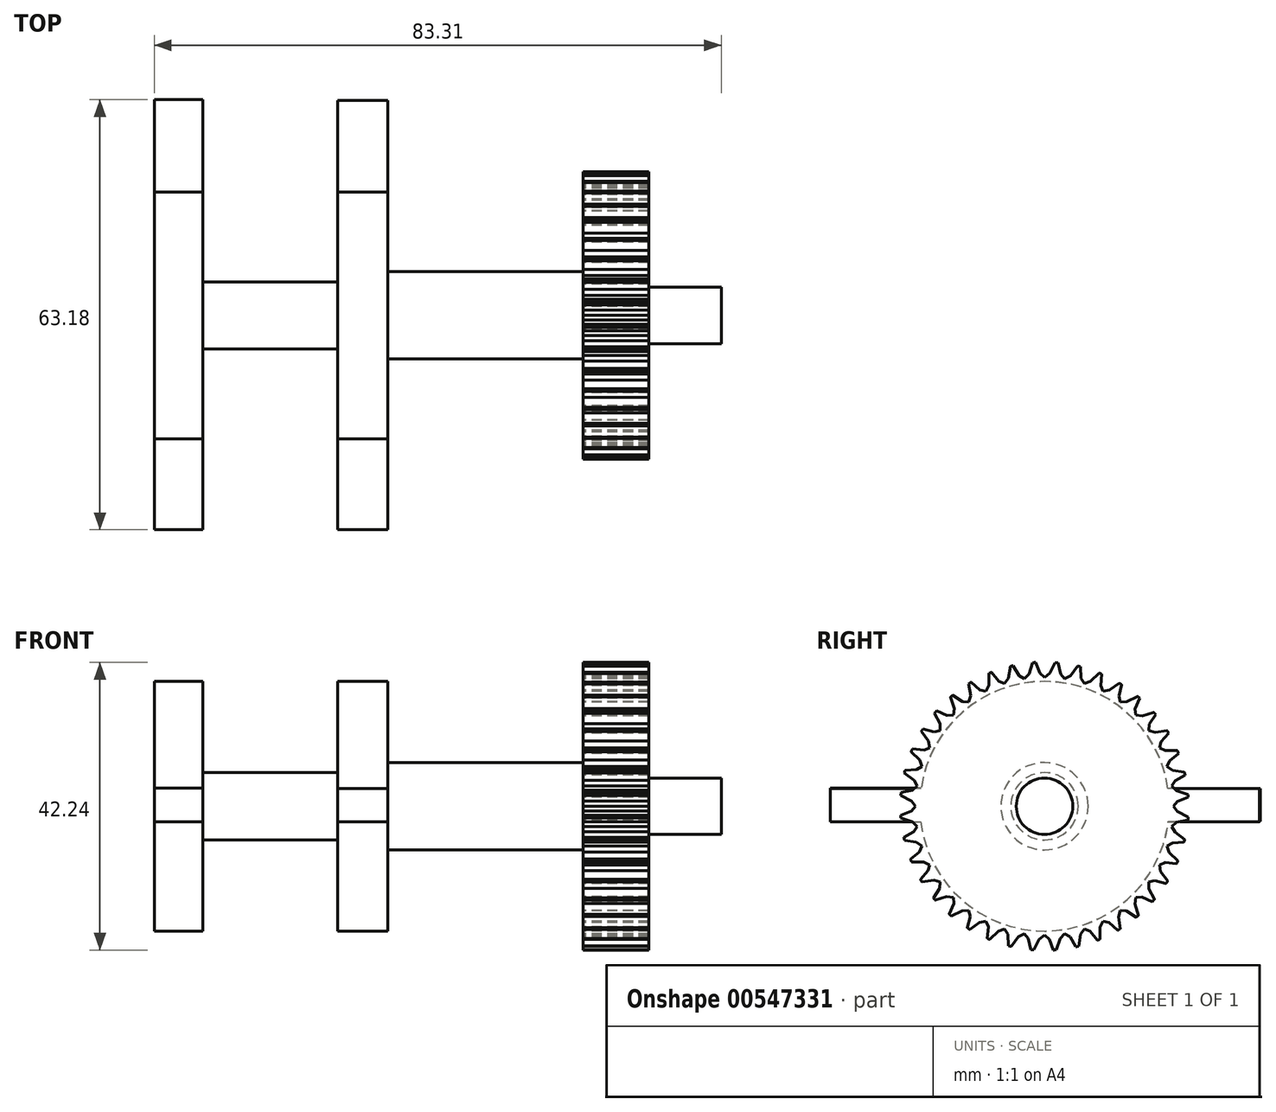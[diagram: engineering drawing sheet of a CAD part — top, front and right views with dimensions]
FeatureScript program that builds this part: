
annotation { "Feature Type Name" : "Feature", "Feature Type Description" : "" }
export const myFeature = defineFeature(function(context is Context, id is Id, definition is map)
    precondition{}
    {
        {
            var Q0;
            Q0=qCreatedBy(makeId("Right.planeOp"),FACE);
            var sketch = newSketch(context, id + "F0", { "sketchPlane" : qUnion([Q0])});
            skCircle(sketch, "E0", {"center": v(0, 0) * mm, "radius": 20.47 * mm});
            skLineSegment(sketch, "E1", {"start": v(0, -20.47) * mm, "end": v(0, -32.87) * mm});
            skLineSegment(sketch, "E2", {"start": v(0, -32.87) * mm, "end": v(-4.43, -32.81) * mm});
            skLineSegment(sketch, "E3", {"start": v(-4.43, -32.81) * mm, "end": v(-4.43, -19.99) * mm});
            skLineSegment(sketch, "E4.MirrorCS", {"start": v(0, 32.87) * mm, "end": v(-4.43, 32.81) * mm});
            skLineSegment(sketch, "E5.MirrorCS", {"start": v(-4.43, 32.81) * mm, "end": v(-4.43, 19.99) * mm});
            skLineSegment(sketch, "E6.MirrorCS", {"start": v(0, 20.47) * mm, "end": v(0, 32.87) * mm});
            skSolve(sketch);
        }
        {
            var Q0;
            {var subQ0=sQuery(id+"F0.wireOp",EDGE,"E0");var subQ1=makeQuery(id+"F0.imprint","INTERSECT",VERTEX,{"derivedFrom":[subQ0,sQuery(id+"F0.wireOp",EDGE,"ybv6XF9e-yQJ6-GcxN-1k9M-g7d4zqfCFwmI")]});Q0=makeQuery(id+"F0.imprint","IMPRINT",FACE,{"disambiguationData":[TD([[makeQuery(id+"F0.imprint","IMPRINT",EDGE,{"disambiguationData":[TD([[subQ1,1.0]])],"derivedFrom":subQ0}),1.0]])]});}
            var Q1;
            {var subQ0=sQuery(id+"F0.wireOp",EDGE,"ybv6XF9e-yQJ6-GcxN-1k9M-g7d4zqfCFwmI");Q1=makeQuery(id+"F0.imprint","IMPRINT",FACE,{"disambiguationData":[TD([[makeQuery(id+"F0.imprint","IMPRINT",EDGE,{"derivedFrom":subQ0}),-1.0]])]});}
            var Q2;
            {var subQ0=sQuery(id+"F0.wireOp",EDGE,"E1");Q2=makeQuery(id+"F0.imprint","IMPRINT",FACE,{"disambiguationData":[TD([[makeQuery(id+"F0.imprint","IMPRINT",EDGE,{"derivedFrom":subQ0}),-1.0]])]});}
            var Q3;
            Q3=makeQuery(id+"F0.imprint","IMPRINT",FACE,{"disambiguationData":[TD([[makeQuery(id+"F0.imprint","IMPRINT",EDGE,{"derivedFrom":sQuery(id+"F0.wireOp",EDGE,"E4.MirrorCS")}),1.0]])]});
            extrude(context, id + "F1", {"entities" : qUnion([Q0, Q1, Q2, Q3]), "depth" : 5.08 * mm, "offsetDistance" : 25.4 * mm});
        }
        {
            var Q0;
            Q0=makeQuery(id+"F1.opExtrude","CAP_FACE",FACE,{"disambiguationData":[OSD([sQuery(id+"F0.wireOp",EDGE,"E0"),sQuery(id+"F0.wireOp",EDGE,"ybv6XF9e-yQJ6-GcxN-1k9M-g7d4zqfCFwmI"),sQuery(id+"F0.wireOp",EDGE,"egRvkigp-FsvL-QF5D-I4YD-MoUuUeyJkvTS"),sQuery(id+"F0.wireOp",EDGE,"ktJIH1Pw-zPiB-Zv6z-c4OE-IvtrcdQjdgDW"),sQuery(id+"F0.wireOp",EDGE,"E1"),sQuery(id+"F0.wireOp",EDGE,"E2"),sQuery(id+"F0.wireOp",EDGE,"E3")])],"isStart":false});
            var sketch = newSketch(context, id + "F2", { "sketchPlane" : qUnion([Q0])});
            skCircle(sketch, "E7", {"center": v(0, 0) * mm, "radius": 22.86 * mm});
            skSolve(sketch);
        }
        {
            var Q0;
            {var subQ1=sQuery(id+"F0.wireOp",EDGE,"ybv6XF9e-yQJ6-GcxN-1k9M-g7d4zqfCFwmI");var subQ7=sQuery(id+"F0.wireOp",EDGE,"E0");var subQ8=makeQuery(id+"F1.opExtrude","CAP_EDGE",EDGE,{"disambiguationData":[OSD([subQ7]),TDD([makeQuery(id+"F0.imprint","IMPRINT",EDGE,{"disambiguationData":[TD([[makeQuery(id+"F0.imprint","INTERSECT",VERTEX,{"derivedFrom":[subQ7,subQ1]}),-1.0]])],"derivedFrom":subQ7})])],"isStart":false});Q0=makeQuery(id+"F2.imprint","IMPRINT",FACE,{"disambiguationData":[TD([[makeQuery(id+"F2.imprint","IMPRINT",EDGE,{"derivedFrom":subQ8}),-1.0]])]});}
            var Q1;
            {var subQ0=sQuery(id+"F0.wireOp",EDGE,"ybv6XF9e-yQJ6-GcxN-1k9M-g7d4zqfCFwmI");var subQ1=sQuery(id+"F0.wireOp",EDGE,"E0");var subQ3=makeQuery(id+"F1.opExtrude","CAP_EDGE",EDGE,{"disambiguationData":[OSD([subQ1]),TDD([makeQuery(id+"F0.imprint","IMPRINT",EDGE,{"disambiguationData":[TD([[makeQuery(id+"F0.imprint","INTERSECT",VERTEX,{"derivedFrom":[subQ1,subQ0]}),-1.0]])],"derivedFrom":subQ1})])],"isStart":false});Q1=makeQuery(id+"F2.imprint","IMPRINT",FACE,{"disambiguationData":[TD([[makeQuery(id+"F2.imprint","IMPRINT",EDGE,{"derivedFrom":subQ3}),1.0]])]});}
            var Q2;
            {var subQ1=sQuery(id+"F0.wireOp",EDGE,"ktJIH1Pw-zPiB-Zv6z-c4OE-IvtrcdQjdgDW");var subQ7=sQuery(id+"F0.wireOp",EDGE,"E0");var subQ8=makeQuery(id+"F1.opExtrude","CAP_EDGE",EDGE,{"disambiguationData":[OSD([subQ7]),TDD([makeQuery(id+"F0.imprint","IMPRINT",EDGE,{"disambiguationData":[TD([[makeQuery(id+"F0.imprint","INTERSECT",VERTEX,{"derivedFrom":[subQ7,subQ1]}),1.0]])],"derivedFrom":subQ7})])],"isStart":false});Q2=makeQuery(id+"F2.imprint","IMPRINT",FACE,{"disambiguationData":[TD([[makeQuery(id+"F2.imprint","IMPRINT",EDGE,{"derivedFrom":subQ8}),-1.0]])]});}
            extrude(context, id + "F3", {"entities" : qUnion([Q0, Q1, Q2]), "operationType" : NewBodyOperationType.ADD, "depth" : 5.84 * mm, "offsetDistance" : 25.4 * mm});
        }
        {
            var Q0;
            Q0=makeQuery(id+"F3.opExtrude","CAP_FACE",FACE,{"disambiguationData":[OSD([sQuery(id+"F2.wireOp",EDGE,"E7")])],"isStart":false});
            var sketch = newSketch(context, id + "F4", { "sketchPlane" : qUnion([Q0])});
            skSolve(sketch);
        }
        {
            var Q0;
            Q0=makeQuery(id+"F1.opExtrude","CAP_FACE",FACE,{"disambiguationData":[OSD([sQuery(id+"F0.wireOp",EDGE,"E0"),sQuery(id+"F0.wireOp",EDGE,"ybv6XF9e-yQJ6-GcxN-1k9M-g7d4zqfCFwmI"),sQuery(id+"F0.wireOp",EDGE,"egRvkigp-FsvL-QF5D-I4YD-MoUuUeyJkvTS"),sQuery(id+"F0.wireOp",EDGE,"ktJIH1Pw-zPiB-Zv6z-c4OE-IvtrcdQjdgDW"),sQuery(id+"F0.wireOp",EDGE,"E1"),sQuery(id+"F0.wireOp",EDGE,"E2"),sQuery(id+"F0.wireOp",EDGE,"E3")])],"isStart":true});
            var sketch = newSketch(context, id + "F5", { "sketchPlane" : qUnion([Q0])});
            skCircle(sketch, "E8", {"center": v(0, 0) * mm, "radius": 4.15 * mm});
            skSolve(sketch);
        }
        {
            var Q0;
            Q0=makeQuery(id+"F5.imprint","IMPRINT",FACE,{"disambiguationData":[TD([[makeQuery(id+"F5.imprint","IMPRINT",EDGE,{"derivedFrom":sQuery(id+"F5.wireOp",EDGE,"E8")}),1.0]])]});
            extrude(context, id + "F6", {"entities" : qUnion([Q0]), "operationType" : NewBodyOperationType.ADD, "depth" : 26.92 * mm, "offsetDistance" : 25.4 * mm});
        }
        {
            var Q0;
            Q0=makeQuery(id+"F6.opExtrude","CAP_FACE",FACE,{"disambiguationData":[OSD([sQuery(id+"F5.wireOp",EDGE,"E8")])],"isStart":false});
            var sketch = newSketch(context, id + "F7", { "sketchPlane" : qUnion([Q0])});
            skCircle(sketch, "E9", {"center": v(0, 0) * mm, "radius": 18.03 * mm});
            skLineSegment(sketch, "E10", {"start": v(0, 18.03) * mm, "end": v(0, 39.42) * mm});
            skLineSegment(sketch, "E11", {"start": v(0, 39.42) * mm, "end": v(4.15, 42.4) * mm});
            skLineSegment(sketch, "E12", {"start": v(4.15, 42.4) * mm, "end": v(4.15, 17.54) * mm});
            skLineSegment(sketch, "E13", {"start": v(0, -18.03) * mm, "end": v(0, -39.5) * mm});
            skLineSegment(sketch, "E14", {"start": v(0, -39.5) * mm, "end": v(4.79, -37.15) * mm});
            skLineSegment(sketch, "E15", {"start": v(4.79, -37.15) * mm, "end": v(4.79, -17.38) * mm});
            skSolve(sketch);
        }
        {
            var Q0;
            Q0=makeQuery(id+"F7.imprint","IMPRINT",FACE,{"disambiguationData":[TD([[makeQuery(id+"F7.imprint","IMPRINT",EDGE,{"derivedFrom":makeQuery(id+"F6.opExtrude","CAP_EDGE",EDGE,{"disambiguationData":[OSD([sQuery(id+"F5.wireOp",EDGE,"E8")])],"isStart":false})}),-1.0]])]});
            var Q1;
            {var subQ0=sQuery(id+"F7.wireOp",EDGE,"E10");Q1=makeQuery(id+"F7.imprint","IMPRINT",FACE,{"disambiguationData":[TD([[makeQuery(id+"F7.imprint","IMPRINT",EDGE,{"derivedFrom":subQ0}),-1.0]])]});}
            var Q2;
            {var subQ0=sQuery(id+"F7.wireOp",EDGE,"E13");Q2=makeQuery(id+"F7.imprint","IMPRINT",FACE,{"disambiguationData":[TD([[makeQuery(id+"F7.imprint","IMPRINT",EDGE,{"derivedFrom":subQ0}),1.0]])]});}
            extrude(context, id + "F8", {"entities" : qUnion([Q0, Q1, Q2]), "operationType" : NewBodyOperationType.ADD, "oppositeDirection" : true, "depth" : 6.35 * mm, "offsetDistance" : 25.4 * mm});
        }
        {
            var Q0;
            {var subQ0=sQuery(id+"F5.wireOp",EDGE,"E8");Q0=makeQuery(id+"F8.boolean.opBoolean","MERGE",FACE,{"derivedFrom":[makeQuery(id+"F6.opExtrude","CAP_FACE",FACE,{"disambiguationData":[OSD([subQ0])],"isStart":false}),makeQuery(id+"F8.opExtrude","CAP_FACE",FACE,{"disambiguationData":[OSD([subQ0,sQuery(id+"F7.wireOp",EDGE,"E9"),sQuery(id+"F7.wireOp",EDGE,"E10"),sQuery(id+"F7.wireOp",EDGE,"E11"),sQuery(id+"F7.wireOp",EDGE,"E12"),sQuery(id+"F7.wireOp",EDGE,"E13"),sQuery(id+"F7.wireOp",EDGE,"E14"),sQuery(id+"F7.wireOp",EDGE,"E15")])],"isStart":true})]});}
            var sketch = newSketch(context, id + "F9", { "sketchPlane" : qUnion([Q0])});
            skCircle(sketch, "E16", {"center": v(0, 0) * mm, "radius": 4.15 * mm});
            skSolve(sketch);
        }
        {
            var Q0;
            Q0=makeQuery(id+"F9.imprint","IMPRINT",FACE,{"disambiguationData":[TD([[makeQuery(id+"F9.imprint","IMPRINT",EDGE,{"derivedFrom":sQuery(id+"F9.wireOp",EDGE,"E16")}),1.0]])]});
            extrude(context, id + "F10", {"entities" : qUnion([Q0]), "operationType" : NewBodyOperationType.ADD, "depth" : 25.4 * mm, "offsetDistance" : 25.4 * mm});
        }
        {
            var Q0;
            Q0=qCreatedBy(makeId("Front.planeOp"),FACE);
            var sketch = newSketch(context, id + "F11", { "sketchPlane" : qUnion([Q0])});
            skLineSegment(sketch, "E17.bottom", {"start": v(-72.04, 32.49) * mm, "end": v(12.18, 32.49) * mm});
            skLineSegment(sketch, "E17.top", {"start": v(-72.04, 43.92) * mm, "end": v(12.18, 43.92) * mm});
            skLineSegment(sketch, "E17.left", {"start": v(-72.04, 32.49) * mm, "end": v(-72.04, 43.92) * mm});
            skLineSegment(sketch, "E17.right", {"start": v(12.18, 32.49) * mm, "end": v(12.18, 43.92) * mm});
            skLineSegment(sketch, "E18.bottom", {"start": v(-70.54, -53.54) * mm, "end": v(14.29, -53.54) * mm});
            skLineSegment(sketch, "E18.top", {"start": v(-70.54, -32.79) * mm, "end": v(14.29, -32.79) * mm});
            skLineSegment(sketch, "E18.left", {"start": v(-70.54, -53.54) * mm, "end": v(-70.54, -32.79) * mm});
            skLineSegment(sketch, "E18.right", {"start": v(14.29, -53.54) * mm, "end": v(14.29, -32.79) * mm});
            skSolve(sketch);
        }
        {
            var Q0;
            Q0=makeQuery(id+"F11.imprint","IMPRINT",FACE,{"disambiguationData":[TD([[makeQuery(id+"F11.imprint","IMPRINT",EDGE,{"derivedFrom":sQuery(id+"F11.wireOp",EDGE,"E17.bottom")}),1.0]])]});
            var Q1;
            Q1=makeQuery(id+"F11.imprint","IMPRINT",FACE,{"disambiguationData":[TD([[makeQuery(id+"F11.imprint","IMPRINT",EDGE,{"derivedFrom":sQuery(id+"F11.wireOp",EDGE,"E18.bottom")}),1.0]])]});
            extrude(context, id + "F12", {"entities" : qUnion([Q0, Q1]), "operationType" : NewBodyOperationType.REMOVE, "depth" : 13.2 * mm, "offsetDistance" : 25.4 * mm});
        }
        {
            var Q0;
            Q0=makeQuery(id+"F10.opExtrude","CAP_FACE",FACE,{"disambiguationData":[OSD([sQuery(id+"F9.wireOp",EDGE,"E16")])],"isStart":false});
            var sketch = newSketch(context, id + "F13", { "sketchPlane" : qUnion([Q0])});
            skCircle(sketch, "E19", {"center": v(0, 0) * mm, "radius": 21.17 * mm});
            skSolve(sketch);
        }
        {
            var Q0;
            Q0=makeQuery(id+"F13.imprint","IMPRINT",FACE,{"disambiguationData":[TD([[makeQuery(id+"F13.imprint","IMPRINT",EDGE,{"derivedFrom":sQuery(id+"F13.wireOp",EDGE,"E19")}),1.0]])]});
            var Q1;
            Q1=makeQuery(id+"F13.imprint","IMPRINT",FACE,{"disambiguationData":[TD([[makeQuery(id+"F13.imprint","IMPRINT",EDGE,{"derivedFrom":makeQuery(id+"F10.opExtrude","CAP_EDGE",EDGE,{"disambiguationData":[OSD([sQuery(id+"F9.wireOp",EDGE,"E16")])],"isStart":false})}),1.0]])]});
            var Q2;
            Q2=sQuery(id+"F13.wireOp",EDGE,"E19");
            extrude(context, id + "F14", {"entities" : qUnion([Q0, Q1]), "operationType" : NewBodyOperationType.ADD, "surfaceEntities" : qUnion([Q2]), "depth" : 9.65 * mm, "offsetDistance" : 25.4 * mm});
        }
        {
            var Q0;
            Q0=makeQuery(id+"F14.opExtrude","CAP_FACE",FACE,{"disambiguationData":[OSD([sQuery(id+"F13.wireOp",EDGE,"E19")])],"isStart":false});
            var sketch = newSketch(context, id + "F15", { "sketchPlane" : qUnion([Q0])});
            skLineSegment(sketch, "E20", {"start": v(-1.58, 21.1) * mm, "end": v(-0.78, 19.54) * mm});
            skLineSegment(sketch, "E21", {"start": v(-0.78, 19.54) * mm, "end": v(0, 18.95) * mm});
            skLineSegment(sketch, "E22", {"start": v(0, 18.95) * mm, "end": v(0.7, 19.54) * mm});
            skLineSegment(sketch, "E23", {"start": v(0.7, 19.54) * mm, "end": v(1.31, 21.12) * mm});
            skLineSegment(sketch, "E24", {"start": v(1.31, 21.12) * mm, "end": v(0.76, 21.54) * mm});
            skLineSegment(sketch, "E25", {"start": v(0.76, 21.54) * mm, "end": v(-0.92, 21.54) * mm});
            skLineSegment(sketch, "E26", {"start": v(-0.92, 21.54) * mm, "end": v(-1.58, 21.1) * mm});
            skSolve(sketch);
        }
        {
            var Q0;
            {var subQ1=sQuery(id+"F15.wireOp",EDGE,"E20");Q0=makeQuery(id+"F15.imprint","IMPRINT",FACE,{"disambiguationData":[TD([[makeQuery(id+"F15.imprint","IMPRINT",EDGE,{"derivedFrom":subQ1}),1.0]])]});}
            extrude(context, id + "F16", {"entities" : qUnion([Q0]), "operationType" : NewBodyOperationType.REMOVE, "oppositeDirection" : true, "depth" : 25.4 * mm, "offsetDistance" : 25.4 * mm});
        }
        {
            var Q0;
            Q0=makeQuery(id+"F16.boolean.opBoolean","COPY",FACE,{"derivedFrom":makeQuery(id+"F16.opExtrude","SWEPT_FACE",FACE,{"disambiguationData":[OSD([sQuery(id+"F15.wireOp",EDGE,"E20")])]})});
            var Q1;
            Q1=makeQuery(id+"F16.boolean.opBoolean","COPY",FACE,{"derivedFrom":makeQuery(id+"F16.opExtrude","SWEPT_FACE",FACE,{"disambiguationData":[OSD([sQuery(id+"F15.wireOp",EDGE,"E22")])]})});
            var Q2;
            Q2=makeQuery(id+"F16.boolean.opBoolean","COPY",FACE,{"derivedFrom":makeQuery(id+"F16.opExtrude","SWEPT_FACE",FACE,{"disambiguationData":[OSD([sQuery(id+"F15.wireOp",EDGE,"E23")])]})});
            var Q3;
            Q3=makeQuery(id+"F16.boolean.opBoolean","COPY",FACE,{"derivedFrom":makeQuery(id+"F16.opExtrude","SWEPT_FACE",FACE,{"disambiguationData":[OSD([sQuery(id+"F15.wireOp",EDGE,"E21")])]})});
            var Q4;
            Q4=makeQuery(id+"F14.opExtrude","SWEPT_FACE",FACE,{"disambiguationData":[OSD([sQuery(id+"F13.wireOp",EDGE,"E19")])]});
            circularPattern(context, id + "F17", {"patternType" : PatternType.FACE, "faces" : qUnion([Q0, Q1, Q2, Q3]), "axis" : qUnion([Q4]), "angle" : 360 * degree, "instanceCount" : 40, "equalSpace" : true});
        }
        {
            var Q0;
            Q0=makeQuery(id+"F14.opExtrude","CAP_FACE",FACE,{"disambiguationData":[OSD([sQuery(id+"F13.wireOp",EDGE,"E19")])],"isStart":false});
            var sketch = newSketch(context, id + "F18", { "sketchPlane" : qUnion([Q0])});
            skCircle(sketch, "E27", {"center": v(0, 0) * mm, "radius": 6.41 * mm});
            skSolve(sketch);
        }
        {
            var Q0;
            Q0=makeQuery(id+"F18.imprint","IMPRINT",FACE,{"disambiguationData":[TD([[makeQuery(id+"F18.imprint","IMPRINT",EDGE,{"derivedFrom":sQuery(id+"F18.wireOp",EDGE,"E27")}),1.0]])]});
            extrude(context, id + "F19", {"entities" : qUnion([Q0]), "operationType" : NewBodyOperationType.ADD, "depth" : 28.7 * mm, "offsetDistance" : 25.4 * mm});
        }
        {
            var Q0;
            Q0=makeQuery(id+"F19.opExtrude","CAP_FACE",FACE,{"disambiguationData":[OSD([sQuery(id+"F18.wireOp",EDGE,"E27")])],"isStart":false});
            var sketch = newSketch(context, id + "F20", { "sketchPlane" : qUnion([Q0])});
            skCircle(sketch, "E28", {"center": v(0, 0) * mm, "radius": 18.33 * mm});
            skLineSegment(sketch, "E29", {"start": v(18.15, 2.6) * mm, "end": v(31.49, 2.6) * mm});
            skLineSegment(sketch, "E30", {"start": v(31.49, 2.6) * mm, "end": v(31.49, 0) * mm});
            skLineSegment(sketch, "E31", {"start": v(31.49, 0) * mm, "end": v(31.49, -2.27) * mm});
            skLineSegment(sketch, "E32", {"start": v(31.49, -2.27) * mm, "end": v(18.2, -2.27) * mm});
            skLineSegment(sketch, "E33", {"start": v(-18.2, -2.27) * mm, "end": v(-31.6, -2.27) * mm});
            skLineSegment(sketch, "E34", {"start": v(-31.6, -2.27) * mm, "end": v(-31.6, 0) * mm});
            skLineSegment(sketch, "E35", {"start": v(-31.6, 0) * mm, "end": v(-31.6, 2.6) * mm});
            skLineSegment(sketch, "E36", {"start": v(-31.6, 2.6) * mm, "end": v(-18.15, 2.6) * mm});
            skSolve(sketch);
        }
        {
            var Q0;
            Q0=makeQuery(id+"F20.imprint","IMPRINT",FACE,{"disambiguationData":[TD([[makeQuery(id+"F20.imprint","IMPRINT",EDGE,{"derivedFrom":makeQuery(id+"F19.opExtrude","CAP_EDGE",EDGE,{"disambiguationData":[OSD([sQuery(id+"F18.wireOp",EDGE,"E27")])],"isStart":false})}),1.0]])]});
            var Q1;
            Q1=makeQuery(id+"F20.imprint","IMPRINT",FACE,{"disambiguationData":[TD([[makeQuery(id+"F20.imprint","IMPRINT",EDGE,{"derivedFrom":sQuery(id+"F20.wireOp",EDGE,"E28")}),1.0]])]});
            extrude(context, id + "F21", {"entities" : qUnion([Q0, Q1]), "operationType" : NewBodyOperationType.ADD, "depth" : 6.6 * mm, "offsetDistance" : 25.4 * mm});
        }
        {
            var Q0;
            Q0=qSketchRegion(id+"F20",true);
            extrude(context, id + "F22", {"entities" : qUnion([Q0]), "operationType" : NewBodyOperationType.ADD, "depth" : 7.37 * mm, "offsetDistance" : 25.4 * mm});
        }
        {
            var Q0;
            Q0=makeQuery(id+"F22.opExtrude","CAP_FACE",FACE,{"disambiguationData":[OSD([sQuery(id+"F20.wireOp",EDGE,"E28"),sQuery(id+"F20.wireOp",EDGE,"E29"),sQuery(id+"F20.wireOp",EDGE,"E30"),sQuery(id+"F20.wireOp",EDGE,"E31"),sQuery(id+"F20.wireOp",EDGE,"E32"),sQuery(id+"F20.wireOp",EDGE,"E33"),sQuery(id+"F20.wireOp",EDGE,"E34"),sQuery(id+"F20.wireOp",EDGE,"E35"),sQuery(id+"F20.wireOp",EDGE,"E36")])],"isStart":false});
            var sketch = newSketch(context, id + "F23", { "sketchPlane" : qUnion([Q0])});
            skCircle(sketch, "E37", {"center": v(0, 0) * mm, "radius": 4.95 * mm});
            skSolve(sketch);
        }
        {
            var Q0;
            Q0=makeQuery(id+"F23.imprint","IMPRINT",FACE,{"disambiguationData":[TD([[makeQuery(id+"F23.imprint","IMPRINT",EDGE,{"derivedFrom":sQuery(id+"F23.wireOp",EDGE,"E37")}),1.0]])]});
            extrude(context, id + "F24", {"entities" : qUnion([Q0]), "operationType" : NewBodyOperationType.ADD, "depth" : 19.8 * mm, "offsetDistance" : 25.4 * mm});
        }
        {
            var Q0;
            Q0=makeQuery(id+"F24.opExtrude","CAP_FACE",FACE,{"disambiguationData":[OSD([sQuery(id+"F23.wireOp",EDGE,"E37")])],"isStart":false});
            var sketch = newSketch(context, id + "F25", { "sketchPlane" : qUnion([Q0])});
            skCircle(sketch, "E38", {"center": v(0, 0) * mm, "radius": 18.33 * mm});
            skLineSegment(sketch, "E39", {"start": v(-18.19, -2.25) * mm, "end": v(-31.7, -2.25) * mm});
            skLineSegment(sketch, "E40", {"start": v(-31.7, -2.25) * mm, "end": v(-31.7, 2.63) * mm});
            skLineSegment(sketch, "E41", {"start": v(-31.7, 2.63) * mm, "end": v(-18.14, 2.63) * mm});
            skLineSegment(sketch, "E42", {"start": v(18.13, 2.64) * mm, "end": v(31.48, 2.64) * mm});
            skLineSegment(sketch, "E43", {"start": v(31.48, 2.64) * mm, "end": v(31.48, -2.26) * mm});
            skLineSegment(sketch, "E44", {"start": v(31.48, -2.26) * mm, "end": v(18.19, -2.26) * mm});
            skSolve(sketch);
        }
        {
            var Q0;
            Q0=makeQuery(id+"F25.imprint","IMPRINT",FACE,{"disambiguationData":[TD([[makeQuery(id+"F25.imprint","IMPRINT",EDGE,{"derivedFrom":makeQuery(id+"F24.opExtrude","CAP_EDGE",EDGE,{"disambiguationData":[OSD([sQuery(id+"F23.wireOp",EDGE,"E37")])],"isStart":false})}),1.0]])]});
            var Q1;
            Q1=makeQuery(id+"F25.imprint","IMPRINT",FACE,{"disambiguationData":[TD([[makeQuery(id+"F25.imprint","IMPRINT",EDGE,{"derivedFrom":makeQuery(id+"F24.opExtrude","CAP_EDGE",EDGE,{"disambiguationData":[OSD([sQuery(id+"F23.wireOp",EDGE,"E37")])],"isStart":false})}),-1.0]])]});
            var Q2;
            {var subQ0=sQuery(id+"F25.wireOp",EDGE,"E39");Q2=makeQuery(id+"F25.imprint","IMPRINT",FACE,{"disambiguationData":[TD([[makeQuery(id+"F25.imprint","IMPRINT",EDGE,{"derivedFrom":subQ0}),-1.0]])]});}
            var Q3;
            {var subQ0=sQuery(id+"F25.wireOp",EDGE,"E42");Q3=makeQuery(id+"F25.imprint","IMPRINT",FACE,{"disambiguationData":[TD([[makeQuery(id+"F25.imprint","IMPRINT",EDGE,{"derivedFrom":subQ0}),-1.0]])]});}
            extrude(context, id + "F26", {"entities" : qUnion([Q0, Q1, Q2, Q3]), "operationType" : NewBodyOperationType.ADD, "depth" : 7.11 * mm, "offsetDistance" : 25.4 * mm});
        }
        {
            var Q0;
            Q0=makeQuery(id+"F3.opExtrude","CAP_FACE",FACE,{"disambiguationData":[OSD([sQuery(id+"F2.wireOp",EDGE,"E7")])],"isStart":false});
            var sketch = newSketch(context, id + "F27", { "sketchPlane" : qUnion([Q0])});
            skCircle(sketch, "E45", {"center": v(0, 15.57) * mm, "radius": 3.64 * mm});
            skCircle(sketch, "E46", {"center": v(0, 15.57) * mm, "radius": 2.28 * mm});
            skSolve(sketch);
        }
        {
            var Q0;
            Q0=makeQuery(id+"F27.imprint","IMPRINT",FACE,{"disambiguationData":[TD([[makeQuery(id+"F27.imprint","IMPRINT",EDGE,{"derivedFrom":sQuery(id+"F27.wireOp",EDGE,"E45")}),1.0]])]});
            extrude(context, id + "F28", {"entities" : qUnion([Q0]), "operationType" : NewBodyOperationType.ADD, "depth" : 7.62 * mm, "offsetDistance" : 25.4 * mm});
        }
        {
            var Q0;
            Q0=makeQuery(id+"F28.opExtrude","CAP_FACE",FACE,{"disambiguationData":[OSD([sQuery(id+"F27.wireOp",EDGE,"E45"),sQuery(id+"F27.wireOp",EDGE,"E46")])],"isStart":false});
            extrude(context, id + "F29", {"entities" : qUnion([Q0]), "operationType" : NewBodyOperationType.ADD, "depth" : 9.14 * mm, "offsetDistance" : 25.4 * mm});
        }
        {
            var Q0;
            Q0=makeQuery(id+"F29.opExtrude","CAP_FACE",FACE,{"disambiguationData":[OSD([sQuery(id+"F27.wireOp",EDGE,"E45"),sQuery(id+"F27.wireOp",EDGE,"E46")])],"isStart":false});
            var sketch = newSketch(context, id + "F30", { "sketchPlane" : qUnion([Q0])});
            skCircle(sketch, "E47", {"center": v(0, 0) * mm, "radius": 39.49 * mm});
            skSolve(sketch);
        }
        {
            var Q0;
            Q0=makeQuery(id+"F30.imprint","IMPRINT",FACE,{"disambiguationData":[TD([[makeQuery(id+"F30.imprint","IMPRINT",EDGE,{"derivedFrom":makeQuery(id+"F29.opExtrude","CAP_EDGE",EDGE,{"disambiguationData":[OSD([sQuery(id+"F27.wireOp",EDGE,"E46")])],"isStart":false})}),1.0]])]});
            var Q1;
            Q1=makeQuery(id+"F30.imprint","IMPRINT",FACE,{"disambiguationData":[TD([[makeQuery(id+"F30.imprint","IMPRINT",EDGE,{"derivedFrom":makeQuery(id+"F29.opExtrude","CAP_EDGE",EDGE,{"disambiguationData":[OSD([sQuery(id+"F27.wireOp",EDGE,"E45")])],"isStart":false})}),1.0]])]});
            var Q2;
            Q2=makeQuery(id+"F30.imprint","IMPRINT",FACE,{"disambiguationData":[TD([[makeQuery(id+"F30.imprint","IMPRINT",EDGE,{"derivedFrom":sQuery(id+"F30.wireOp",EDGE,"E47")}),1.0]])]});
            extrude(context, id + "F31", {"entities" : qUnion([Q0, Q1, Q2]), "operationType" : NewBodyOperationType.REMOVE, "oppositeDirection" : true, "depth" : 69.34 * mm, "offsetDistance" : 25.4 * mm});
        }
    });
